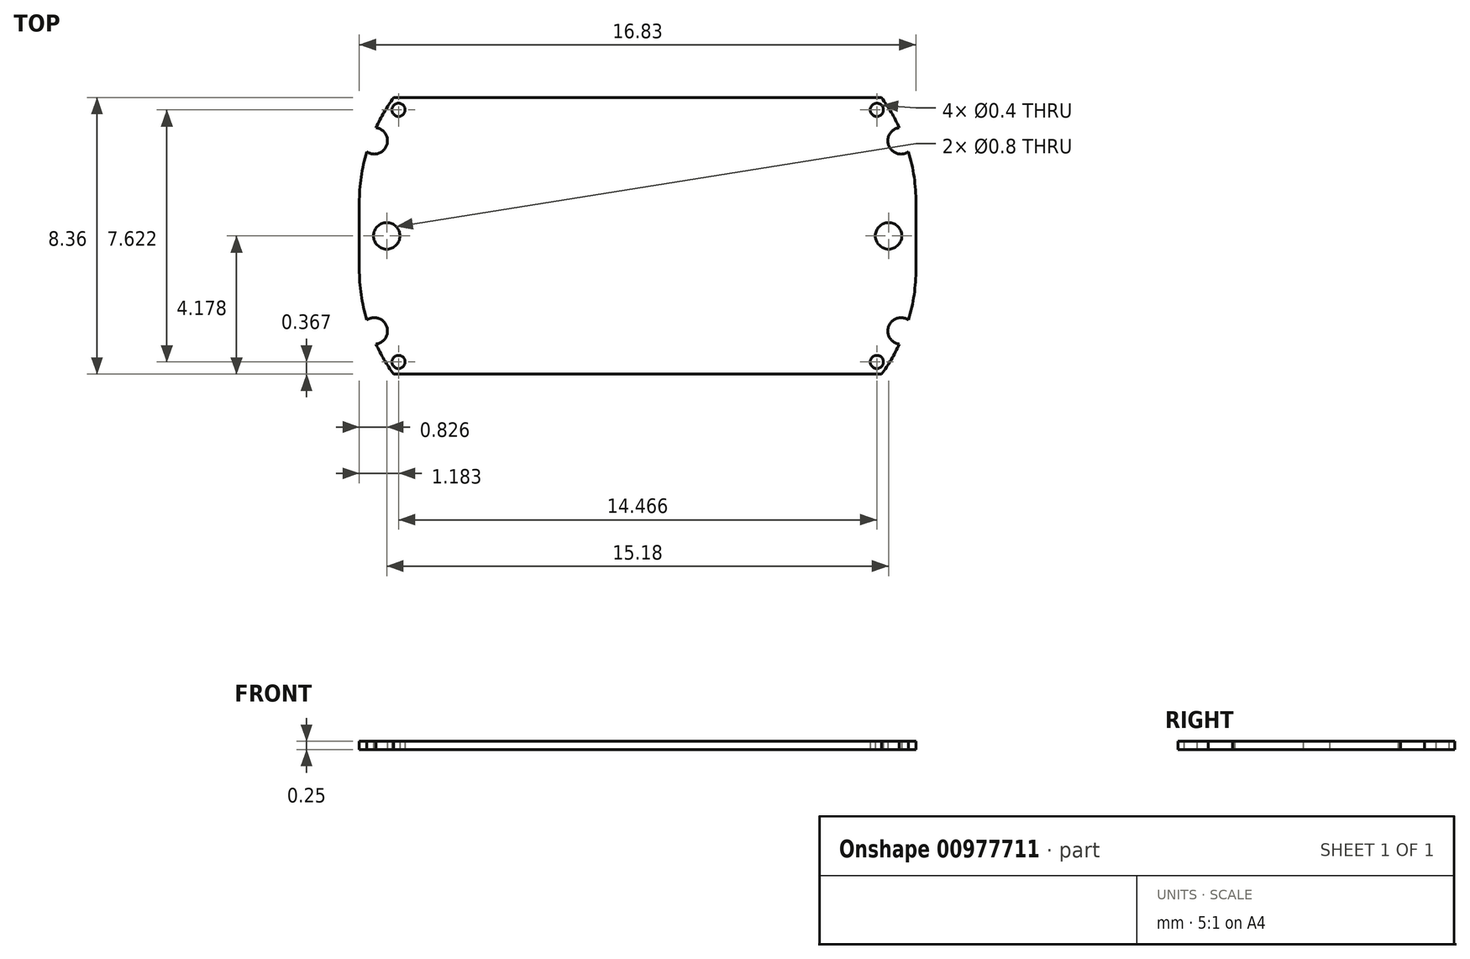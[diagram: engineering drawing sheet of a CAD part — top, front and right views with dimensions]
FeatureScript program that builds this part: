
annotation { "Feature Type Name" : "Feature", "Feature Type Description" : "" }
export const myFeature = defineFeature(function(context is Context, id is Id, definition is map)
    precondition{}
    {
        {
            var Q0;
            Q0=qCreatedBy(makeId("Top.planeOp"),FACE);
            var sketch = newSketch(context, id + "F0", { "sketchPlane" : qUnion([Q0])});
            skLineSegment(sketch, "E0", {"start": v(-7.38, 4.06) * mm, "end": v(7.47, 4.06) * mm});
            skLineSegment(sketch, "E1", {"start": v(-7.38, -4.3) * mm, "end": v(7.47, -4.3) * mm});
            skLineSegment(sketch, "E2", {"start": v(-8.42, -0.12) * mm, "end": v(-8.42, 0.88) * mm});
            skArc(sketch, "E3", {"start": v(-7.38, 4.06) * mm, "mid": v(-7.67, 3.62) * mm, "end": v(-7.92, 3.15) * mm});
            skLineSegment(sketch, "E4", {"start": v(0, -0.12) * mm, "end": v(0, 5.97) * mm, "construction": true});
            skCircle(sketch, "E5", {"center": v(-7.24, 3.69) * mm, "radius": 0.2 * mm});
            skArc(sketch, "E6", {"start": v(-8.2, 2.42) * mm, "mid": v(-7.6, 2.6) * mm, "end": v(-7.92, 3.15) * mm});
            skArc(sketch, "E7.trimOffspring", {"start": v(-8.2, 2.42) * mm, "mid": v(-8.37, 1.66) * mm, "end": v(-8.42, 0.88) * mm});
            skCircle(sketch, "E8.MirrorC", {"center": v(-7.24, -3.93) * mm, "radius": 0.2 * mm});
            skArc(sketch, "E9.MirrorCS", {"start": v(-7.38, -4.3) * mm, "mid": v(-7.67, -3.86) * mm, "end": v(-7.92, -3.4) * mm});
            skArc(sketch, "E10.MirrorCS", {"start": v(-8.2, -2.66) * mm, "mid": v(-7.6, -2.85) * mm, "end": v(-7.92, -3.4) * mm});
            skArc(sketch, "E11.MirrorCS", {"start": v(-8.2, -2.66) * mm, "mid": v(-8.37, -1.9) * mm, "end": v(-8.42, -1.12) * mm});
            skLineSegment(sketch, "E12.MirrorCS", {"start": v(-8.42, -0.12) * mm, "end": v(-8.42, -1.12) * mm});
            skLineSegment(sketch, "E13.MirrorCS", {"start": v(8.41, -0.12) * mm, "end": v(8.41, 0.88) * mm});
            skLineSegment(sketch, "E14.MirrorCS", {"start": v(8.41, -0.12) * mm, "end": v(8.41, -1.12) * mm});
            skArc(sketch, "E15.MirrorCS", {"start": v(7.37, 4.06) * mm, "mid": v(7.66, 3.62) * mm, "end": v(7.9, 3.15) * mm});
            skArc(sketch, "E16.MirrorCS", {"start": v(7.37, -4.3) * mm, "mid": v(7.66, -3.86) * mm, "end": v(7.9, -3.4) * mm});
            skArc(sketch, "E17.MirrorCS", {"start": v(8.19, 2.42) * mm, "mid": v(7.59, 2.6) * mm, "end": v(7.9, 3.15) * mm});
            skCircle(sketch, "E18.MirrorC", {"center": v(7.23, 3.69) * mm, "radius": 0.2 * mm});
            skCircle(sketch, "E19.MirrorC", {"center": v(7.23, -3.93) * mm, "radius": 0.2 * mm});
            skArc(sketch, "E20.MirrorCS", {"start": v(8.19, -2.66) * mm, "mid": v(7.59, -2.85) * mm, "end": v(7.9, -3.4) * mm});
            skArc(sketch, "E21.MirrorCS", {"start": v(8.19, 2.42) * mm, "mid": v(8.36, 1.66) * mm, "end": v(8.41, 0.88) * mm});
            skArc(sketch, "E22.MirrorCS", {"start": v(8.19, -2.66) * mm, "mid": v(8.36, -1.9) * mm, "end": v(8.41, -1.12) * mm});
            skCircle(sketch, "E23", {"center": v(-7.6, -0.12) * mm, "radius": 0.4 * mm});
            skCircle(sketch, "E24.MirrorC", {"center": v(7.59, -0.12) * mm, "radius": 0.4 * mm});
            skSolve(sketch);
        }
        {
            var Q0;
            Q0=makeQuery(id+"F0.imprint","IMPRINT",FACE,{"disambiguationData":[TD([[makeQuery(id+"F0.imprint","IMPRINT",EDGE,{"derivedFrom":sQuery(id+"F0.wireOp",EDGE,"E2")}),-1.0]])]});
            var Q1;
            Q1=sQuery(id+"F0.wireOp",EDGE,"E0");
            var Q2;
            Q2=sQuery(id+"F0.wireOp",EDGE,"E1");
            var Q3;
            Q3=sQuery(id+"F0.wireOp",EDGE,"E2");
            var Q4;
            Q4=sQuery(id+"F0.wireOp",EDGE,"E3");
            var Q5;
            Q5=sQuery(id+"F0.wireOp",EDGE,"E5");
            var Q6;
            Q6=sQuery(id+"F0.wireOp",EDGE,"E6");
            var Q7;
            Q7=sQuery(id+"F0.wireOp",EDGE,"E7.trimOffspring");
            var Q8;
            Q8=sQuery(id+"F0.wireOp",EDGE,"E8.MirrorC");
            var Q9;
            Q9=sQuery(id+"F0.wireOp",EDGE,"E9.MirrorCS");
            var Q10;
            Q10=sQuery(id+"F0.wireOp",EDGE,"E10.MirrorCS");
            var Q11;
            Q11=sQuery(id+"F0.wireOp",EDGE,"E11.MirrorCS");
            var Q12;
            Q12=sQuery(id+"F0.wireOp",EDGE,"E12.MirrorCS");
            var Q13;
            Q13=sQuery(id+"F0.wireOp",EDGE,"E13.MirrorCS");
            var Q14;
            Q14=sQuery(id+"F0.wireOp",EDGE,"E14.MirrorCS");
            var Q15;
            Q15=sQuery(id+"F0.wireOp",EDGE,"E15.MirrorCS");
            var Q16;
            Q16=sQuery(id+"F0.wireOp",EDGE,"E16.MirrorCS");
            var Q17;
            Q17=sQuery(id+"F0.wireOp",EDGE,"E17.MirrorCS");
            var Q18;
            Q18=sQuery(id+"F0.wireOp",EDGE,"E18.MirrorC");
            var Q19;
            Q19=sQuery(id+"F0.wireOp",EDGE,"E19.MirrorC");
            var Q20;
            Q20=sQuery(id+"F0.wireOp",EDGE,"E20.MirrorCS");
            var Q21;
            Q21=sQuery(id+"F0.wireOp",EDGE,"E21.MirrorCS");
            var Q22;
            Q22=sQuery(id+"F0.wireOp",EDGE,"E22.MirrorCS");
            var Q23;
            Q23=sQuery(id+"F0.wireOp",EDGE,"E23");
            var Q24;
            Q24=sQuery(id+"F0.wireOp",EDGE,"E24.MirrorC");
            extrude(context, id + "F1", {"entities" : qUnion([Q0]), "surfaceEntities" : qUnion([Q1, Q2, Q3, Q4, Q5, Q6, Q7, Q8, Q9, Q10, Q11, Q12, Q13, Q14, Q15, Q16, Q17, Q18, Q19, Q20, Q21, Q22, Q23, Q24]), "depth" : .25 * mm, "offsetDistance" : 25 * mm});
        }
    });
